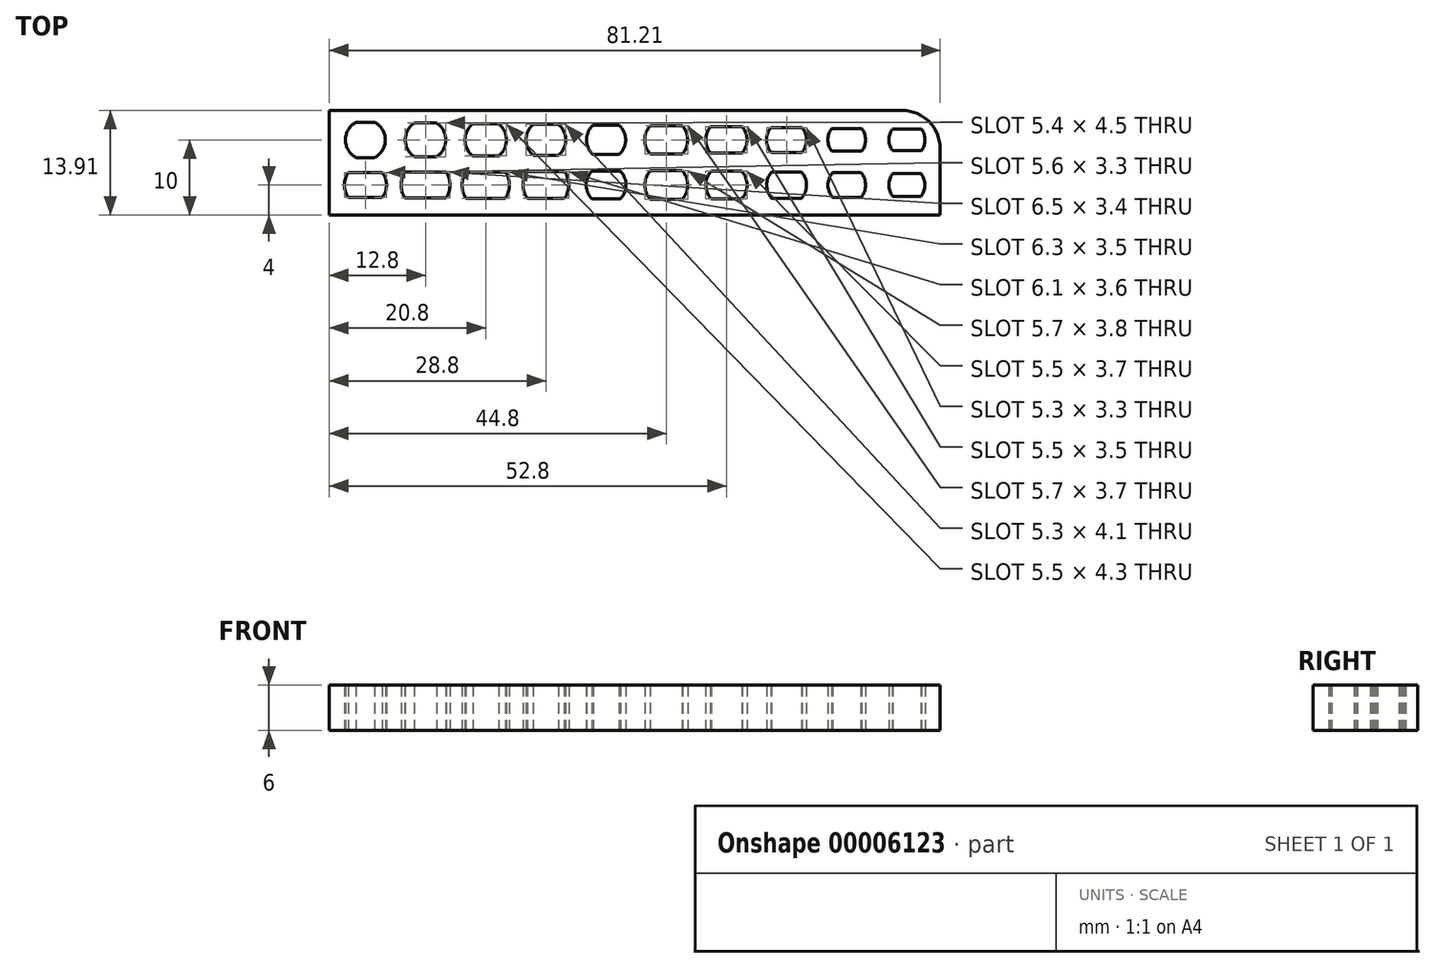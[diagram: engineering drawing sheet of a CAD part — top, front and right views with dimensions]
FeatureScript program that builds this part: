
annotation { "Feature Type Name" : "Feature", "Feature Type Description" : "" }
export const myFeature = defineFeature(function(context is Context, id is Id, definition is map)
    precondition{}
    {
        {
            var Q0;
            Q0=qCreatedBy(makeId("Top.planeOp"),FACE);
            var sketch = newSketch(context, id + "F0", { "sketchPlane" : qUnion([Q0])});
            skLineSegment(sketch, "E0.left", {"start": v(-38, 3.9) * mm, "end": v(-38, -3.9) * mm, "construction": true});
            skLineSegment(sketch, "E0.right", {"start": v(38, 4) * mm, "end": v(38, -4) * mm, "construction": true});
            skLineSegment(sketch, "E1", {"start": v(-38, 0) * mm, "end": v(38, 0) * mm, "construction": true});
            skPoint(sketch, "E1.endSnap0", {"position": v(38, 0) * mm});
            skPoint(sketch, "E2", {"position": v(0, 0) * mm});
            skCircle(sketch, "E3", {"center": v(-36, 0) * mm, "radius": 2.65 * mm});
            skLineSegment(sketch, "E4", {"start": v(-37.22, 2.35) * mm, "end": v(-34.78, 2.35) * mm});
            skLineSegment(sketch, "E5", {"start": v(-37.22, -2.35) * mm, "end": v(-34.78, -2.35) * mm});
            skCircle(sketch, "E6", {"center": v(-28, 0) * mm, "radius": 2.7 * mm});
            skLineSegment(sketch, "E7", {"start": v(-29.5, 2.25) * mm, "end": v(-26.5, 2.25) * mm});
            skLineSegment(sketch, "E8", {"start": v(-29.5, -2.25) * mm, "end": v(-26.5, -2.25) * mm});
            skCircle(sketch, "E9", {"center": v(-20, 0) * mm, "radius": 2.75 * mm});
            skLineSegment(sketch, "E10", {"start": v(-21.71, 2.15) * mm, "end": v(-18.29, 2.15) * mm});
            skLineSegment(sketch, "E11", {"start": v(-21.71, -2.15) * mm, "end": v(-18.29, -2.15) * mm});
            skCircle(sketch, "E12", {"center": v(-12, 0) * mm, "radius": 2.65 * mm});
            skLineSegment(sketch, "E13", {"start": v(-13.68, 2.05) * mm, "end": v(-10.32, 2.05) * mm});
            skLineSegment(sketch, "E14", {"start": v(-13.68, -2.05) * mm, "end": v(-10.32, -2.05) * mm});
            skCircle(sketch, "E15", {"center": v(-4, 0) * mm, "radius": 2.6 * mm});
            skLineSegment(sketch, "E16", {"start": v(-5.72, 1.95) * mm, "end": v(-2.28, 1.95) * mm});
            skLineSegment(sketch, "E17", {"start": v(-5.72, -1.95) * mm, "end": v(-2.28, -1.95) * mm});
            skCircle(sketch, "E18", {"center": v(4, 0) * mm, "radius": 2.85 * mm});
            skLineSegment(sketch, "E19", {"start": v(1.83, 1.85) * mm, "end": v(6.17, 1.85) * mm});
            skLineSegment(sketch, "E20", {"start": v(1.83, -1.85) * mm, "end": v(6.17, -1.85) * mm});
            skCircle(sketch, "E21", {"center": v(12, 0) * mm, "radius": 2.75 * mm});
            skLineSegment(sketch, "E22", {"start": v(9.88, 1.75) * mm, "end": v(14.12, 1.75) * mm});
            skLineSegment(sketch, "E23", {"start": v(9.88, -1.75) * mm, "end": v(14.12, -1.75) * mm});
            skCircle(sketch, "E24", {"center": v(20, 0) * mm, "radius": 2.65 * mm});
            skLineSegment(sketch, "E25", {"start": v(17.93, 1.65) * mm, "end": v(22.07, 1.65) * mm});
            skLineSegment(sketch, "E26", {"start": v(17.93, -1.65) * mm, "end": v(22.07, -1.65) * mm});
            skCircle(sketch, "E27", {"center": v(28, 0) * mm, "radius": 2.5 * mm});
            skLineSegment(sketch, "E28", {"start": v(26, 1.5) * mm, "end": v(30, 1.5) * mm});
            skLineSegment(sketch, "E29", {"start": v(26, -1.5) * mm, "end": v(30, -1.5) * mm});
            skCircle(sketch, "E30", {"center": v(36, 0) * mm, "radius": 2.4 * mm});
            skLineSegment(sketch, "E31", {"start": v(34.08, 1.45) * mm, "end": v(37.92, 1.45) * mm});
            skLineSegment(sketch, "E32", {"start": v(34.08, -1.45) * mm, "end": v(37.92, -1.45) * mm});
            skLineSegment(sketch, "E33.left", {"start": v(-38, -2) * mm, "end": v(-38, -10) * mm, "construction": true});
            skLineSegment(sketch, "E33.right", {"start": v(38, -2) * mm, "end": v(38, -10) * mm, "construction": true});
            skLineSegment(sketch, "E34", {"start": v(-38, -6) * mm, "end": v(38, -6) * mm, "construction": true});
            skPoint(sketch, "E34.endSnap0", {"position": v(38, -6) * mm});
            skPoint(sketch, "E35", {"position": v(0, -6) * mm});
            skCircle(sketch, "E36", {"center": v(-36, -6) * mm, "radius": 2.8 * mm});
            skLineSegment(sketch, "E37", {"start": v(-38.26, -4.35) * mm, "end": v(-33.74, -4.35) * mm});
            skLineSegment(sketch, "E38", {"start": v(-38.26, -7.65) * mm, "end": v(-33.74, -7.65) * mm});
            skCircle(sketch, "E39", {"center": v(-28, -6) * mm, "radius": 3.25 * mm});
            skLineSegment(sketch, "E40", {"start": v(-30.77, -4.3) * mm, "end": v(-25.23, -4.3) * mm});
            skLineSegment(sketch, "E41", {"start": v(-30.77, -7.7) * mm, "end": v(-25.23, -7.7) * mm});
            skCircle(sketch, "E42", {"center": v(-20, -6) * mm, "radius": 3.15 * mm});
            skLineSegment(sketch, "E43", {"start": v(-22.62, -4.25) * mm, "end": v(-17.38, -4.25) * mm});
            skLineSegment(sketch, "E44", {"start": v(-22.62, -7.75) * mm, "end": v(-17.38, -7.75) * mm});
            skCircle(sketch, "E45", {"center": v(-12, -6) * mm, "radius": 3.05 * mm});
            skLineSegment(sketch, "E46", {"start": v(-14.46, -4.2) * mm, "end": v(-9.54, -4.2) * mm});
            skLineSegment(sketch, "E47", {"start": v(-14.46, -7.8) * mm, "end": v(-9.54, -7.8) * mm});
            skCircle(sketch, "E48", {"center": v(-4, -6) * mm, "radius": 2.65 * mm});
            skLineSegment(sketch, "E49", {"start": v(-5.9, -4.15) * mm, "end": v(-2.1, -4.15) * mm});
            skLineSegment(sketch, "E50", {"start": v(-5.9, -7.85) * mm, "end": v(-2.1, -7.85) * mm});
            skCircle(sketch, "E51", {"center": v(4, -6) * mm, "radius": 2.85 * mm});
            skLineSegment(sketch, "E52", {"start": v(1.88, -4.1) * mm, "end": v(6.12, -4.1) * mm});
            skLineSegment(sketch, "E53", {"start": v(1.88, -7.9) * mm, "end": v(6.12, -7.9) * mm});
            skCircle(sketch, "E54", {"center": v(12, -6) * mm, "radius": 2.75 * mm});
            skLineSegment(sketch, "E55", {"start": v(9.97, -4.15) * mm, "end": v(14.03, -4.15) * mm});
            skLineSegment(sketch, "E56", {"start": v(9.97, -7.85) * mm, "end": v(14.03, -7.85) * mm});
            skCircle(sketch, "E57", {"center": v(20, -6) * mm, "radius": 2.65 * mm});
            skLineSegment(sketch, "E58", {"start": v(18.01, -4.25) * mm, "end": v(21.99, -4.25) * mm});
            skLineSegment(sketch, "E59", {"start": v(18.01, -7.75) * mm, "end": v(21.99, -7.75) * mm});
            skCircle(sketch, "E60", {"center": v(28, -6) * mm, "radius": 2.5 * mm});
            skLineSegment(sketch, "E61", {"start": v(26.12, -4.35) * mm, "end": v(29.88, -4.35) * mm});
            skLineSegment(sketch, "E62", {"start": v(26.12, -7.65) * mm, "end": v(29.88, -7.65) * mm});
            skCircle(sketch, "E63", {"center": v(36, -6) * mm, "radius": 2.4 * mm});
            skLineSegment(sketch, "E64", {"start": v(34.12, -4.5) * mm, "end": v(37.88, -4.5) * mm});
            skLineSegment(sketch, "E65", {"start": v(34.12, -7.5) * mm, "end": v(37.88, -7.5) * mm});
            skLineSegment(sketch, "E66.bottom", {"start": v(-40.8, 3.9) * mm, "end": v(35.4, 3.9) * mm});
            skLineSegment(sketch, "E66.top", {"start": v(-40.8, -10) * mm, "end": v(40.4, -10) * mm});
            skLineSegment(sketch, "E66.left", {"start": v(-40.8, 3.9) * mm, "end": v(-40.8, -10) * mm});
            skLineSegment(sketch, "E66.right", {"start": v(40.4, -1.1) * mm, "end": v(40.4, -10) * mm});
            skPoint(sketch, "E67.visualSharp", {"position": v(40.4, 3.9) * mm});
            skArc(sketch, "E67.filletArc", {"start": v(40.4, -1.1) * mm, "mid": v(38.94, 2.44) * mm, "end": v(35.4, 3.9) * mm});
            skSolve(sketch);
        }
        {
            var Q0;
            {var subQ0=sQuery(id+"F0.wireOp",EDGE,"E7");Q0=makeQuery(id+"F0.imprint","IMPRINT",FACE,{"disambiguationData":[TD([[makeQuery(id+"F0.imprint","IMPRINT",EDGE,{"derivedFrom":subQ0}),1.0]])]});}
            var Q1;
            {var subQ0=sQuery(id+"F0.wireOp",EDGE,"E8");Q1=makeQuery(id+"F0.imprint","IMPRINT",FACE,{"disambiguationData":[TD([[makeQuery(id+"F0.imprint","IMPRINT",EDGE,{"derivedFrom":subQ0}),-1.0]])]});}
            var Q2;
            {var subQ0=sQuery(id+"F0.wireOp",EDGE,"E5");Q2=makeQuery(id+"F0.imprint","IMPRINT",FACE,{"disambiguationData":[TD([[makeQuery(id+"F0.imprint","IMPRINT",EDGE,{"derivedFrom":subQ0}),-1.0]])]});}
            var Q3;
            {var subQ0=sQuery(id+"F0.wireOp",EDGE,"E37");Q3=makeQuery(id+"F0.imprint","IMPRINT",FACE,{"disambiguationData":[TD([[makeQuery(id+"F0.imprint","IMPRINT",EDGE,{"derivedFrom":subQ0}),1.0]])]});}
            var Q4;
            {var subQ0=sQuery(id+"F0.wireOp",EDGE,"E41");Q4=makeQuery(id+"F0.imprint","IMPRINT",FACE,{"disambiguationData":[TD([[makeQuery(id+"F0.imprint","IMPRINT",EDGE,{"derivedFrom":subQ0}),-1.0]])]});}
            var Q5;
            {var subQ0=sQuery(id+"F0.wireOp",EDGE,"E40");Q5=makeQuery(id+"F0.imprint","IMPRINT",FACE,{"disambiguationData":[TD([[makeQuery(id+"F0.imprint","IMPRINT",EDGE,{"derivedFrom":subQ0}),1.0]])]});}
            var Q6;
            {var subQ0=sQuery(id+"F0.wireOp",EDGE,"E43");Q6=makeQuery(id+"F0.imprint","IMPRINT",FACE,{"disambiguationData":[TD([[makeQuery(id+"F0.imprint","IMPRINT",EDGE,{"derivedFrom":subQ0}),1.0]])]});}
            var Q7;
            {var subQ0=sQuery(id+"F0.wireOp",EDGE,"E46");Q7=makeQuery(id+"F0.imprint","IMPRINT",FACE,{"disambiguationData":[TD([[makeQuery(id+"F0.imprint","IMPRINT",EDGE,{"derivedFrom":subQ0}),1.0]])]});}
            var Q8;
            {var subQ0=sQuery(id+"F0.wireOp",EDGE,"E49");Q8=makeQuery(id+"F0.imprint","IMPRINT",FACE,{"disambiguationData":[TD([[makeQuery(id+"F0.imprint","IMPRINT",EDGE,{"derivedFrom":subQ0}),1.0]])]});}
            var Q9;
            {var subQ0=sQuery(id+"F0.wireOp",EDGE,"E52");Q9=makeQuery(id+"F0.imprint","IMPRINT",FACE,{"disambiguationData":[TD([[makeQuery(id+"F0.imprint","IMPRINT",EDGE,{"derivedFrom":subQ0}),1.0]])]});}
            var Q10;
            {var subQ0=sQuery(id+"F0.wireOp",EDGE,"E55");Q10=makeQuery(id+"F0.imprint","IMPRINT",FACE,{"disambiguationData":[TD([[makeQuery(id+"F0.imprint","IMPRINT",EDGE,{"derivedFrom":subQ0}),1.0]])]});}
            var Q11;
            {var subQ0=sQuery(id+"F0.wireOp",EDGE,"E58");Q11=makeQuery(id+"F0.imprint","IMPRINT",FACE,{"disambiguationData":[TD([[makeQuery(id+"F0.imprint","IMPRINT",EDGE,{"derivedFrom":subQ0}),1.0]])]});}
            var Q12;
            {var subQ0=sQuery(id+"F0.wireOp",EDGE,"E61");Q12=makeQuery(id+"F0.imprint","IMPRINT",FACE,{"disambiguationData":[TD([[makeQuery(id+"F0.imprint","IMPRINT",EDGE,{"derivedFrom":subQ0}),1.0]])]});}
            var Q13;
            {var subQ0=sQuery(id+"F0.wireOp",EDGE,"E64");Q13=makeQuery(id+"F0.imprint","IMPRINT",FACE,{"disambiguationData":[TD([[makeQuery(id+"F0.imprint","IMPRINT",EDGE,{"derivedFrom":subQ0}),1.0]])]});}
            var Q14;
            {var subQ0=sQuery(id+"F0.wireOp",EDGE,"E65");Q14=makeQuery(id+"F0.imprint","IMPRINT",FACE,{"disambiguationData":[TD([[makeQuery(id+"F0.imprint","IMPRINT",EDGE,{"derivedFrom":subQ0}),-1.0]])]});}
            var Q15;
            {var subQ0=sQuery(id+"F0.wireOp",EDGE,"E62");Q15=makeQuery(id+"F0.imprint","IMPRINT",FACE,{"disambiguationData":[TD([[makeQuery(id+"F0.imprint","IMPRINT",EDGE,{"derivedFrom":subQ0}),-1.0]])]});}
            var Q16;
            {var subQ0=sQuery(id+"F0.wireOp",EDGE,"E56");Q16=makeQuery(id+"F0.imprint","IMPRINT",FACE,{"disambiguationData":[TD([[makeQuery(id+"F0.imprint","IMPRINT",EDGE,{"derivedFrom":subQ0}),-1.0]])]});}
            var Q17;
            {var subQ0=sQuery(id+"F0.wireOp",EDGE,"E50");Q17=makeQuery(id+"F0.imprint","IMPRINT",FACE,{"disambiguationData":[TD([[makeQuery(id+"F0.imprint","IMPRINT",EDGE,{"derivedFrom":subQ0}),-1.0]])]});}
            var Q18;
            {var subQ0=sQuery(id+"F0.wireOp",EDGE,"E47");Q18=makeQuery(id+"F0.imprint","IMPRINT",FACE,{"disambiguationData":[TD([[makeQuery(id+"F0.imprint","IMPRINT",EDGE,{"derivedFrom":subQ0}),-1.0]])]});}
            var Q19;
            {var subQ0=sQuery(id+"F0.wireOp",EDGE,"E44");Q19=makeQuery(id+"F0.imprint","IMPRINT",FACE,{"disambiguationData":[TD([[makeQuery(id+"F0.imprint","IMPRINT",EDGE,{"derivedFrom":subQ0}),-1.0]])]});}
            var Q20;
            {var subQ0=sQuery(id+"F0.wireOp",EDGE,"E38");Q20=makeQuery(id+"F0.imprint","IMPRINT",FACE,{"disambiguationData":[TD([[makeQuery(id+"F0.imprint","IMPRINT",EDGE,{"derivedFrom":subQ0}),-1.0]])]});}
            var Q21;
            {var subQ0=sQuery(id+"F0.wireOp",EDGE,"E53");Q21=makeQuery(id+"F0.imprint","IMPRINT",FACE,{"disambiguationData":[TD([[makeQuery(id+"F0.imprint","IMPRINT",EDGE,{"derivedFrom":subQ0}),-1.0]])]});}
            var Q22;
            {var subQ0=sQuery(id+"F0.wireOp",EDGE,"E59");Q22=makeQuery(id+"F0.imprint","IMPRINT",FACE,{"disambiguationData":[TD([[makeQuery(id+"F0.imprint","IMPRINT",EDGE,{"derivedFrom":subQ0}),-1.0]])]});}
            var Q23;
            {var subQ0=sQuery(id+"F0.wireOp",EDGE,"E32");Q23=makeQuery(id+"F0.imprint","IMPRINT",FACE,{"disambiguationData":[TD([[makeQuery(id+"F0.imprint","IMPRINT",EDGE,{"derivedFrom":subQ0}),-1.0]])]});}
            var Q24;
            {var subQ0=sQuery(id+"F0.wireOp",EDGE,"E29");Q24=makeQuery(id+"F0.imprint","IMPRINT",FACE,{"disambiguationData":[TD([[makeQuery(id+"F0.imprint","IMPRINT",EDGE,{"derivedFrom":subQ0}),-1.0]])]});}
            var Q25;
            {var subQ0=sQuery(id+"F0.wireOp",EDGE,"E26");Q25=makeQuery(id+"F0.imprint","IMPRINT",FACE,{"disambiguationData":[TD([[makeQuery(id+"F0.imprint","IMPRINT",EDGE,{"derivedFrom":subQ0}),-1.0]])]});}
            var Q26;
            {var subQ0=sQuery(id+"F0.wireOp",EDGE,"E23");Q26=makeQuery(id+"F0.imprint","IMPRINT",FACE,{"disambiguationData":[TD([[makeQuery(id+"F0.imprint","IMPRINT",EDGE,{"derivedFrom":subQ0}),-1.0]])]});}
            var Q27;
            {var subQ0=sQuery(id+"F0.wireOp",EDGE,"E20");Q27=makeQuery(id+"F0.imprint","IMPRINT",FACE,{"disambiguationData":[TD([[makeQuery(id+"F0.imprint","IMPRINT",EDGE,{"derivedFrom":subQ0}),-1.0]])]});}
            var Q28;
            {var subQ0=sQuery(id+"F0.wireOp",EDGE,"E17");Q28=makeQuery(id+"F0.imprint","IMPRINT",FACE,{"disambiguationData":[TD([[makeQuery(id+"F0.imprint","IMPRINT",EDGE,{"derivedFrom":subQ0}),-1.0]])]});}
            var Q29;
            {var subQ0=sQuery(id+"F0.wireOp",EDGE,"E14");Q29=makeQuery(id+"F0.imprint","IMPRINT",FACE,{"disambiguationData":[TD([[makeQuery(id+"F0.imprint","IMPRINT",EDGE,{"derivedFrom":subQ0}),-1.0]])]});}
            var Q30;
            {var subQ0=sQuery(id+"F0.wireOp",EDGE,"E11");Q30=makeQuery(id+"F0.imprint","IMPRINT",FACE,{"disambiguationData":[TD([[makeQuery(id+"F0.imprint","IMPRINT",EDGE,{"derivedFrom":subQ0}),-1.0]])]});}
            var Q31;
            {var subQ0=sQuery(id+"F0.wireOp",EDGE,"E10");Q31=makeQuery(id+"F0.imprint","IMPRINT",FACE,{"disambiguationData":[TD([[makeQuery(id+"F0.imprint","IMPRINT",EDGE,{"derivedFrom":subQ0}),1.0]])]});}
            var Q32;
            {var subQ0=sQuery(id+"F0.wireOp",EDGE,"E13");Q32=makeQuery(id+"F0.imprint","IMPRINT",FACE,{"disambiguationData":[TD([[makeQuery(id+"F0.imprint","IMPRINT",EDGE,{"derivedFrom":subQ0}),1.0]])]});}
            var Q33;
            {var subQ0=sQuery(id+"F0.wireOp",EDGE,"E16");Q33=makeQuery(id+"F0.imprint","IMPRINT",FACE,{"disambiguationData":[TD([[makeQuery(id+"F0.imprint","IMPRINT",EDGE,{"derivedFrom":subQ0}),1.0]])]});}
            var Q34;
            {var subQ0=sQuery(id+"F0.wireOp",EDGE,"E19");Q34=makeQuery(id+"F0.imprint","IMPRINT",FACE,{"disambiguationData":[TD([[makeQuery(id+"F0.imprint","IMPRINT",EDGE,{"derivedFrom":subQ0}),1.0]])]});}
            var Q35;
            {var subQ0=sQuery(id+"F0.wireOp",EDGE,"E22");Q35=makeQuery(id+"F0.imprint","IMPRINT",FACE,{"disambiguationData":[TD([[makeQuery(id+"F0.imprint","IMPRINT",EDGE,{"derivedFrom":subQ0}),1.0]])]});}
            var Q36;
            {var subQ0=sQuery(id+"F0.wireOp",EDGE,"E25");Q36=makeQuery(id+"F0.imprint","IMPRINT",FACE,{"disambiguationData":[TD([[makeQuery(id+"F0.imprint","IMPRINT",EDGE,{"derivedFrom":subQ0}),1.0]])]});}
            var Q37;
            {var subQ0=sQuery(id+"F0.wireOp",EDGE,"E28");Q37=makeQuery(id+"F0.imprint","IMPRINT",FACE,{"disambiguationData":[TD([[makeQuery(id+"F0.imprint","IMPRINT",EDGE,{"derivedFrom":subQ0}),1.0]])]});}
            var Q38;
            {var subQ0=sQuery(id+"F0.wireOp",EDGE,"E31");Q38=makeQuery(id+"F0.imprint","IMPRINT",FACE,{"disambiguationData":[TD([[makeQuery(id+"F0.imprint","IMPRINT",EDGE,{"derivedFrom":subQ0}),1.0]])]});}
            var Q39;
            Q39=makeQuery(id+"F0.imprint","IMPRINT",FACE,{"disambiguationData":[TD([[makeQuery(id+"F0.imprint","IMPRINT",EDGE,{"derivedFrom":sQuery(id+"F0.wireOp",EDGE,"E66.bottom")}),-1.0]])]});
            var Q40;
            {var subQ0=sQuery(id+"F0.wireOp",EDGE,"E4");Q40=makeQuery(id+"F0.imprint","IMPRINT",FACE,{"disambiguationData":[TD([[makeQuery(id+"F0.imprint","IMPRINT",EDGE,{"derivedFrom":subQ0}),1.0]])]});}
            extrude(context, id + "F1", {"entities" : qUnion([Q0, Q1, Q2, Q3, Q4, Q5, Q6, Q7, Q8, Q9, Q10, Q11, Q12, Q13, Q14, Q15, Q16, Q17, Q18, Q19, Q20, Q21, Q22, Q23, Q24, Q25, Q26, Q27, Q28, Q29, Q30, Q31, Q32, Q33, Q34, Q35, Q36, Q37, Q38, Q39, Q40]), "depth" : 6 * mm});
        }
    });
